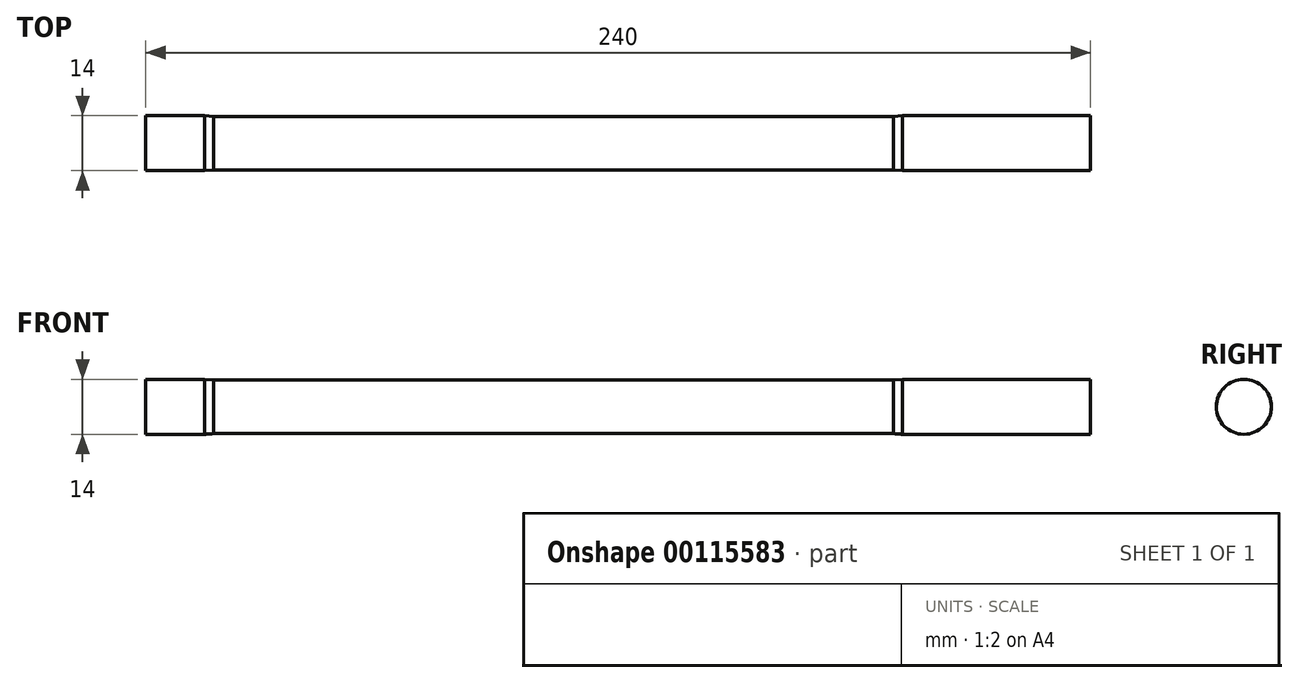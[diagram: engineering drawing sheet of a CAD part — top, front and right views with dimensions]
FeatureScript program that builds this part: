
annotation { "Feature Type Name" : "Feature", "Feature Type Description" : "" }
export const myFeature = defineFeature(function(context is Context, id is Id, definition is map)
    precondition{}
    {
        {
            var Q0;
            Q0=qCreatedBy(makeId("Front.planeOp"),FACE);
            var sketch = newSketch(context, id + "F0", { "sketchPlane" : qUnion([Q0])});
            skLineSegment(sketch, "E0", {"start": v(-97.45, 0) * mm, "end": v(-97.45, 7) * mm});
            skLineSegment(sketch, "E1", {"start": v(-97.45, 7) * mm, "end": v(-82.45, 7) * mm});
            skLineSegment(sketch, "E2", {"start": v(94.83, 7) * mm, "end": v(142.55, 7) * mm});
            skLineSegment(sketch, "E3", {"start": v(142.55, 7) * mm, "end": v(142.55, 0) * mm});
            skLineSegment(sketch, "E4", {"start": v(142.55, 0) * mm, "end": v(-97.45, 0) * mm});
            skLineSegment(sketch, "E5", {"start": v(94.83, 7) * mm, "end": v(92.55, 6.8) * mm});
            skLineSegment(sketch, "E6", {"start": v(92.55, 6.8) * mm, "end": v(-80.17, 6.8) * mm});
            skLineSegment(sketch, "E7", {"start": v(-82.45, 7) * mm, "end": v(-80.17, 6.8) * mm});
            skSolve(sketch);
        }
        {
            var Q0;
            Q0 = qSketchRegion(id + "F0", true);
            var Q1;
            Q1=sQuery(id+"F0.wireOp",EDGE,"E4");
            revolve(context, id + "F1", {"entities" : qUnion([Q0]), "axis" : qUnion([Q1]), "revolveType" : RevolveType.FULL});
        }
    });
